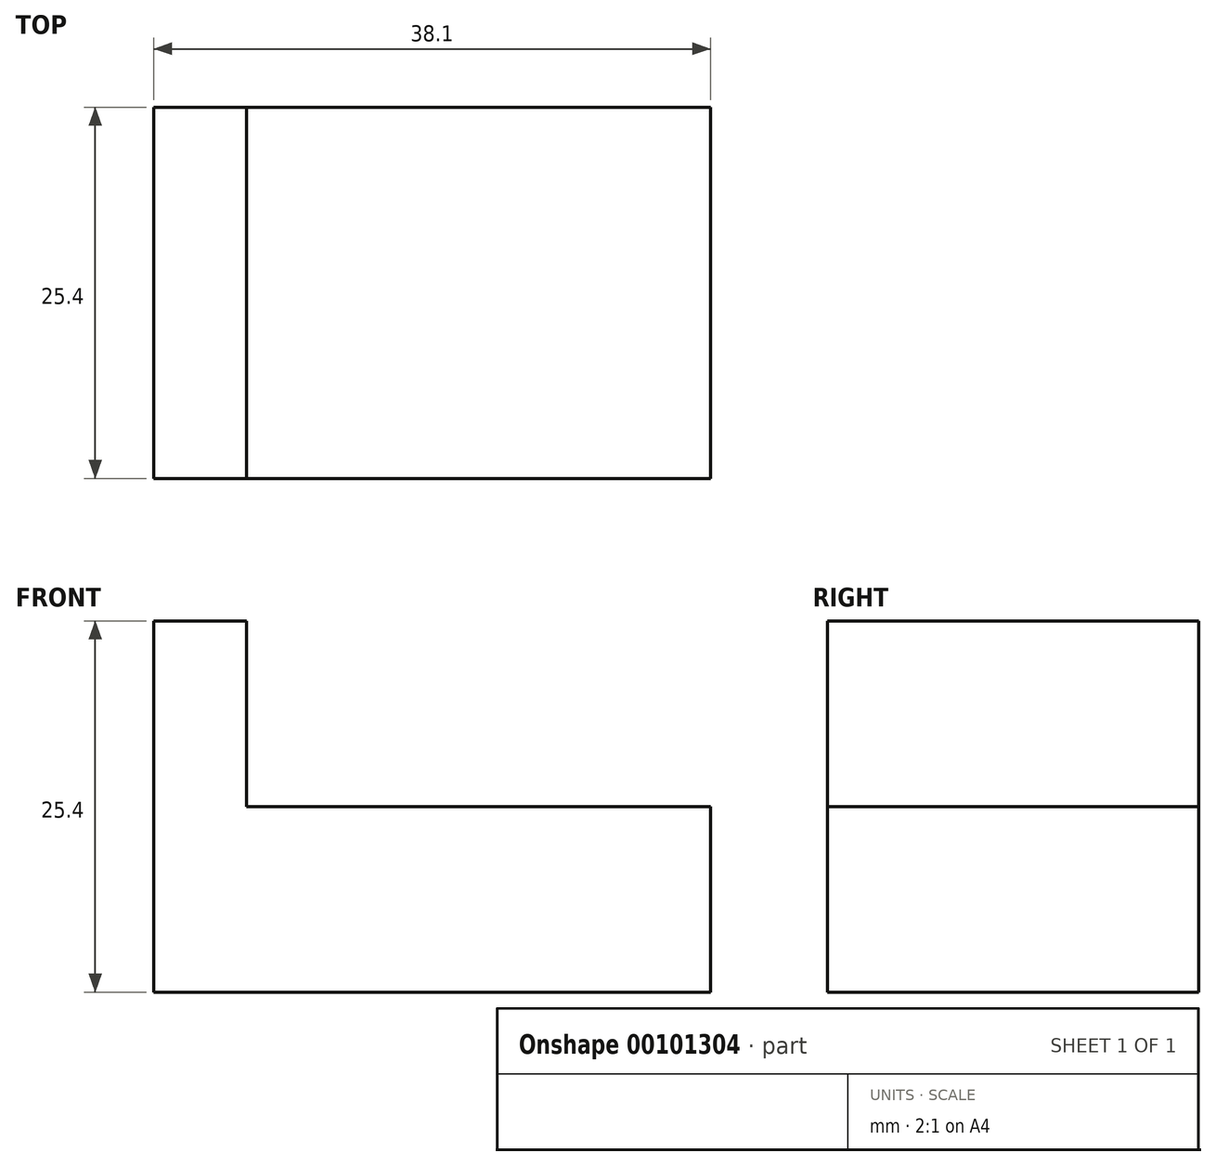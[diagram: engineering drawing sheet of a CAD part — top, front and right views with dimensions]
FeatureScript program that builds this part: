
annotation { "Feature Type Name" : "Feature", "Feature Type Description" : "" }
export const myFeature = defineFeature(function(context is Context, id is Id, definition is map)
    precondition{}
    {
        {
            var Q0;
            Q0=qCreatedBy(makeId("Front.planeOp"),FACE);
            var sketch = newSketch(context, id + "F0", { "sketchPlane" : qUnion([Q0])});
            skLineSegment(sketch, "E0", {"start": v(0, 0) * mm, "end": v(0, 25.4) * mm});
            skLineSegment(sketch, "E1", {"start": v(0, 25.4) * mm, "end": v(6.35, 25.4) * mm});
            skLineSegment(sketch, "E2", {"start": v(6.35, 25.4) * mm, "end": v(6.35, 12.7) * mm});
            skLineSegment(sketch, "E3", {"start": v(6.35, 12.7) * mm, "end": v(38.1, 12.7) * mm});
            skLineSegment(sketch, "E4", {"start": v(38.1, 12.7) * mm, "end": v(38.1, 0) * mm});
            skLineSegment(sketch, "E5", {"start": v(38.1, 0) * mm, "end": v(0, 0) * mm});
            skSolve(sketch);
        }
        {
            var Q0;
            Q0 = qSketchRegion(id + "F0", true);
            extrude(context, id + "F1", {"entities" : qUnion([Q0]), "oppositeDirection" : true, "depth" : 25.4 * mm});
        }
    });
